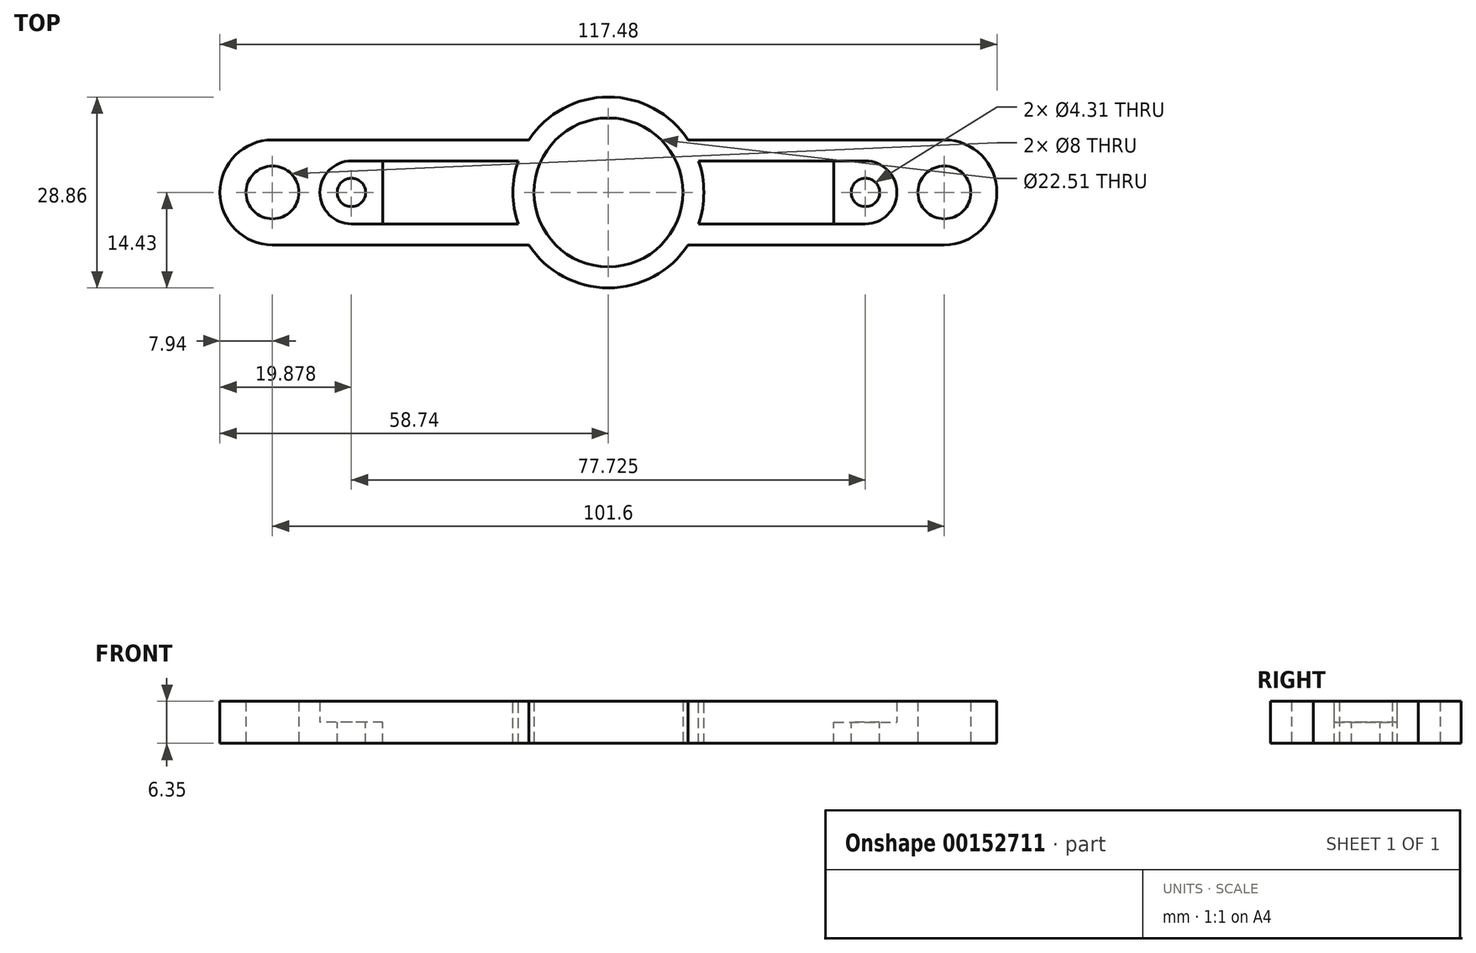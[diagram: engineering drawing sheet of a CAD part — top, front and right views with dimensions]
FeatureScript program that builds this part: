
annotation { "Feature Type Name" : "Feature", "Feature Type Description" : "" }
export const myFeature = defineFeature(function(context is Context, id is Id, definition is map)
    precondition{}
    {
        {
            var Q0;
            Q0=qCreatedBy(makeId("Top.planeOp"),FACE);
            var sketch = newSketch(context, id + "F0", { "sketchPlane" : qUnion([Q0])});
            skCircle(sketch, "E0", {"center": v(0, 0) * mm, "radius": 11.25 * mm});
            skLineSegment(sketch, "E1", {"start": v(-50.8, 0) * mm, "end": v(50.8, 0) * mm, "construction": true});
            skCircle(sketch, "E2", {"center": v(-50.8, 0) * mm, "radius": 4 * mm});
            skCircle(sketch, "E3", {"center": v(50.8, 0) * mm, "radius": 4 * mm});
            skLineSegment(sketch, "E4.bottom", {"start": v(-50.8, 7.94) * mm, "end": v(-12.05, 7.94) * mm});
            skLineSegment(sketch, "E4.top", {"start": v(-50.8, -7.94) * mm, "end": v(-12.05, -7.94) * mm});
            skLineSegment(sketch, "E4.left", {"start": v(-50.8, 7.94) * mm, "end": v(-50.8, -7.94) * mm, "construction": true});
            skLineSegment(sketch, "E5.bottom", {"start": v(12.05, 7.94) * mm, "end": v(50.8, 7.94) * mm});
            skLineSegment(sketch, "E5.top", {"start": v(12.05, -7.94) * mm, "end": v(50.8, -7.94) * mm});
            skLineSegment(sketch, "E5.right", {"start": v(50.8, 7.94) * mm, "end": v(50.8, -7.94) * mm, "construction": true});
            skArc(sketch, "E6", {"start": v(-50.8, 7.94) * mm, "mid": v(-58.74, 0) * mm, "end": v(-50.8, -7.94) * mm});
            skArc(sketch, "E7", {"start": v(50.8, -7.94) * mm, "mid": v(58.74, 0) * mm, "end": v(50.8, 7.94) * mm});
            skArc(sketch, "E8", {"start": v(12.05, 7.94) * mm, "mid": v(0, 14.43) * mm, "end": v(-12.05, 7.94) * mm});
            skArc(sketch, "E9", {"start": v(-12.05, -7.94) * mm, "mid": v(0, -14.43) * mm, "end": v(12.05, -7.94) * mm});
            skSolve(sketch);
        }
        {
            var Q0;
            Q0 = qSketchRegion(id + "F0", true);
            extrude(context, id + "F1", {"entities" : qUnion([Q0]), "depth" : 6.35 * mm});
        }
        {
            var Q0;
            Q0=makeQuery(id+"F1.opExtrude","CAP_FACE",FACE,{"disambiguationData":[OSD([sQuery(id+"F0.wireOp",EDGE,"E0"),sQuery(id+"F0.wireOp",EDGE,"E2"),sQuery(id+"F0.wireOp",EDGE,"E3"),sQuery(id+"F0.wireOp",EDGE,"E4.bottom"),sQuery(id+"F0.wireOp",EDGE,"E4.top"),sQuery(id+"F0.wireOp",EDGE,"E5.bottom"),sQuery(id+"F0.wireOp",EDGE,"E5.top"),sQuery(id+"F0.wireOp",EDGE,"E6"),sQuery(id+"F0.wireOp",EDGE,"E7"),sQuery(id+"F0.wireOp",EDGE,"E8"),sQuery(id+"F0.wireOp",EDGE,"E9")])],"isStart":false});
            var sketch = newSketch(context, id + "F2", { "sketchPlane" : qUnion([Q0])});
            skLineSegment(sketch, "E10.bottom", {"start": v(-13.62, 4.76) * mm, "end": v(-34.1, 4.76) * mm});
            skLineSegment(sketch, "E10.top", {"start": v(-13.62, -4.76) * mm, "end": v(-34.1, -4.76) * mm});
            skLineSegment(sketch, "E10.left", {"start": v(-13.62, 4.76) * mm, "end": v(-13.62, -4.76) * mm, "construction": true});
            skLineSegment(sketch, "E10.right", {"start": v(-34.1, 4.76) * mm, "end": v(-34.1, -4.76) * mm});
            skLineSegment(sketch, "E11.bottom", {"start": v(13.62, 4.76) * mm, "end": v(34.1, 4.76) * mm});
            skLineSegment(sketch, "E11.top", {"start": v(13.62, -4.76) * mm, "end": v(34.1, -4.76) * mm});
            skLineSegment(sketch, "E11.left", {"start": v(13.62, 4.76) * mm, "end": v(13.62, -4.76) * mm, "construction": true});
            skLineSegment(sketch, "E11.right", {"start": v(34.1, 4.76) * mm, "end": v(34.1, -4.76) * mm});
            skLineSegment(sketch, "E12", {"start": v(-50.8, 0) * mm, "end": v(-43.63, 0) * mm, "construction": true});
            skLineSegment(sketch, "E13", {"start": v(-43.63, 0) * mm, "end": v(-34.1, 0) * mm, "construction": true});
            skArc(sketch, "E14", {"start": v(-13.62, 4.76) * mm, "mid": v(-14.43, 0) * mm, "end": v(-13.62, -4.76) * mm});
            skLineSegment(sketch, "E15", {"start": v(34.1, 0) * mm, "end": v(43.63, 0) * mm, "construction": true});
            skLineSegment(sketch, "E16", {"start": v(43.63, 0) * mm, "end": v(50.8, 0) * mm, "construction": true});
            skArc(sketch, "E17", {"start": v(13.62, -4.76) * mm, "mid": v(14.43, 0) * mm, "end": v(13.62, 4.76) * mm});
            skCircle(sketch, "E18", {"center": v(-38.86, 0) * mm, "radius": 2.15 * mm});
            skCircle(sketch, "E19", {"center": v(38.86, 0) * mm, "radius": 2.15 * mm});
            skSolve(sketch);
        }
        {
            var Q0;
            Q0 = qSketchRegion(id + "F2", true);
            var Q1;
            Q1=makeQuery(id+"F1.opExtrude","CAP_FACE",FACE,{"disambiguationData":[OSD([sQuery(id+"F0.wireOp",EDGE,"E0"),sQuery(id+"F0.wireOp",EDGE,"E2"),sQuery(id+"F0.wireOp",EDGE,"E3"),sQuery(id+"F0.wireOp",EDGE,"E4.bottom"),sQuery(id+"F0.wireOp",EDGE,"E4.top"),sQuery(id+"F0.wireOp",EDGE,"E5.bottom"),sQuery(id+"F0.wireOp",EDGE,"E5.top"),sQuery(id+"F0.wireOp",EDGE,"E6"),sQuery(id+"F0.wireOp",EDGE,"E7"),sQuery(id+"F0.wireOp",EDGE,"E8"),sQuery(id+"F0.wireOp",EDGE,"E9")])],"isStart":true});
            extrude(context, id + "F3", {"entities" : qUnion([Q0]), "operationType" : NewBodyOperationType.REMOVE, "endBound" : BoundingType.UP_TO_SURFACE, "oppositeDirection" : true, "endBoundEntityFace" : qUnion([Q1]), "depth" : 25.4 * mm});
        }
        {
            var Q0;
            Q0=makeQuery(id+"F1.opExtrude","CAP_FACE",FACE,{"disambiguationData":[OSD([sQuery(id+"F0.wireOp",EDGE,"E0"),sQuery(id+"F0.wireOp",EDGE,"E2"),sQuery(id+"F0.wireOp",EDGE,"E3"),sQuery(id+"F0.wireOp",EDGE,"E4.bottom"),sQuery(id+"F0.wireOp",EDGE,"E4.top"),sQuery(id+"F0.wireOp",EDGE,"E5.bottom"),sQuery(id+"F0.wireOp",EDGE,"E5.top"),sQuery(id+"F0.wireOp",EDGE,"E6"),sQuery(id+"F0.wireOp",EDGE,"E7"),sQuery(id+"F0.wireOp",EDGE,"E8"),sQuery(id+"F0.wireOp",EDGE,"E9")])],"isStart":false});
            var sketch = newSketch(context, id + "F4", { "sketchPlane" : qUnion([Q0])});
            skLineSegment(sketch, "E20.bottom", {"start": v(-34.1, 4.76) * mm, "end": v(-43.63, 4.76) * mm});
            skLineSegment(sketch, "E20.top", {"start": v(-34.1, -4.76) * mm, "end": v(-43.63, -4.76) * mm});
            skLineSegment(sketch, "E20.left", {"start": v(-34.1, 4.76) * mm, "end": v(-34.1, -4.76) * mm});
            skLineSegment(sketch, "E20.right", {"start": v(-43.63, 4.76) * mm, "end": v(-43.63, -4.76) * mm});
            skPoint(sketch, "E20.middle", {"position": v(-38.86, 0) * mm});
            skLineSegment(sketch, "E21.bottom", {"start": v(34.1, 4.76) * mm, "end": v(43.63, 4.76) * mm});
            skLineSegment(sketch, "E21.top", {"start": v(34.1, -4.76) * mm, "end": v(43.63, -4.76) * mm});
            skLineSegment(sketch, "E21.left", {"start": v(34.1, 4.76) * mm, "end": v(34.1, -4.76) * mm});
            skLineSegment(sketch, "E21.right", {"start": v(43.63, 4.76) * mm, "end": v(43.63, -4.76) * mm});
            skPoint(sketch, "E21.middle", {"position": v(38.86, 0) * mm});
            skSolve(sketch);
        }
        {
            var Q0;
            Q0 = qSketchRegion(id + "F4", true);
            extrude(context, id + "F5", {"entities" : qUnion([Q0]), "operationType" : NewBodyOperationType.REMOVE, "oppositeDirection" : true, "depth" : 3.17 * mm});
        }
        {
            var Q0;
            Q0=makeQuery(id+"F5.boolean.opBoolean","COPY",EDGE,{"derivedFrom":makeQuery(id+"F5.opExtrude","SWEPT_EDGE",EDGE,{"disambiguationData":[OSD([sQuery(id+"F4.wireOp",EDGE,"E20.bottom"),sQuery(id+"F4.wireOp",EDGE,"E20.right")])]})});
            var Q1;
            Q1=makeQuery(id+"F5.boolean.opBoolean","COPY",EDGE,{"derivedFrom":makeQuery(id+"F5.opExtrude","SWEPT_EDGE",EDGE,{"disambiguationData":[OSD([sQuery(id+"F4.wireOp",EDGE,"E20.top"),sQuery(id+"F4.wireOp",EDGE,"E20.right")])]})});
            var Q2;
            Q2=makeQuery(id+"F5.boolean.opBoolean","COPY",EDGE,{"derivedFrom":makeQuery(id+"F5.opExtrude","SWEPT_EDGE",EDGE,{"disambiguationData":[OSD([sQuery(id+"F4.wireOp",EDGE,"E21.bottom"),sQuery(id+"F4.wireOp",EDGE,"E21.right")])]})});
            var Q3;
            Q3=makeQuery(id+"F5.boolean.opBoolean","COPY",EDGE,{"derivedFrom":makeQuery(id+"F5.opExtrude","SWEPT_EDGE",EDGE,{"disambiguationData":[OSD([sQuery(id+"F4.wireOp",EDGE,"E21.top"),sQuery(id+"F4.wireOp",EDGE,"E21.right")])]})});
            fillet(context, id + "F6", {"entities" : qUnion([Q0, Q1, Q2, Q3]), "radius" : 4.76 * mm, "tangentPropagation" : true, "allowEdgeOverflow" : false});
        }
    });
